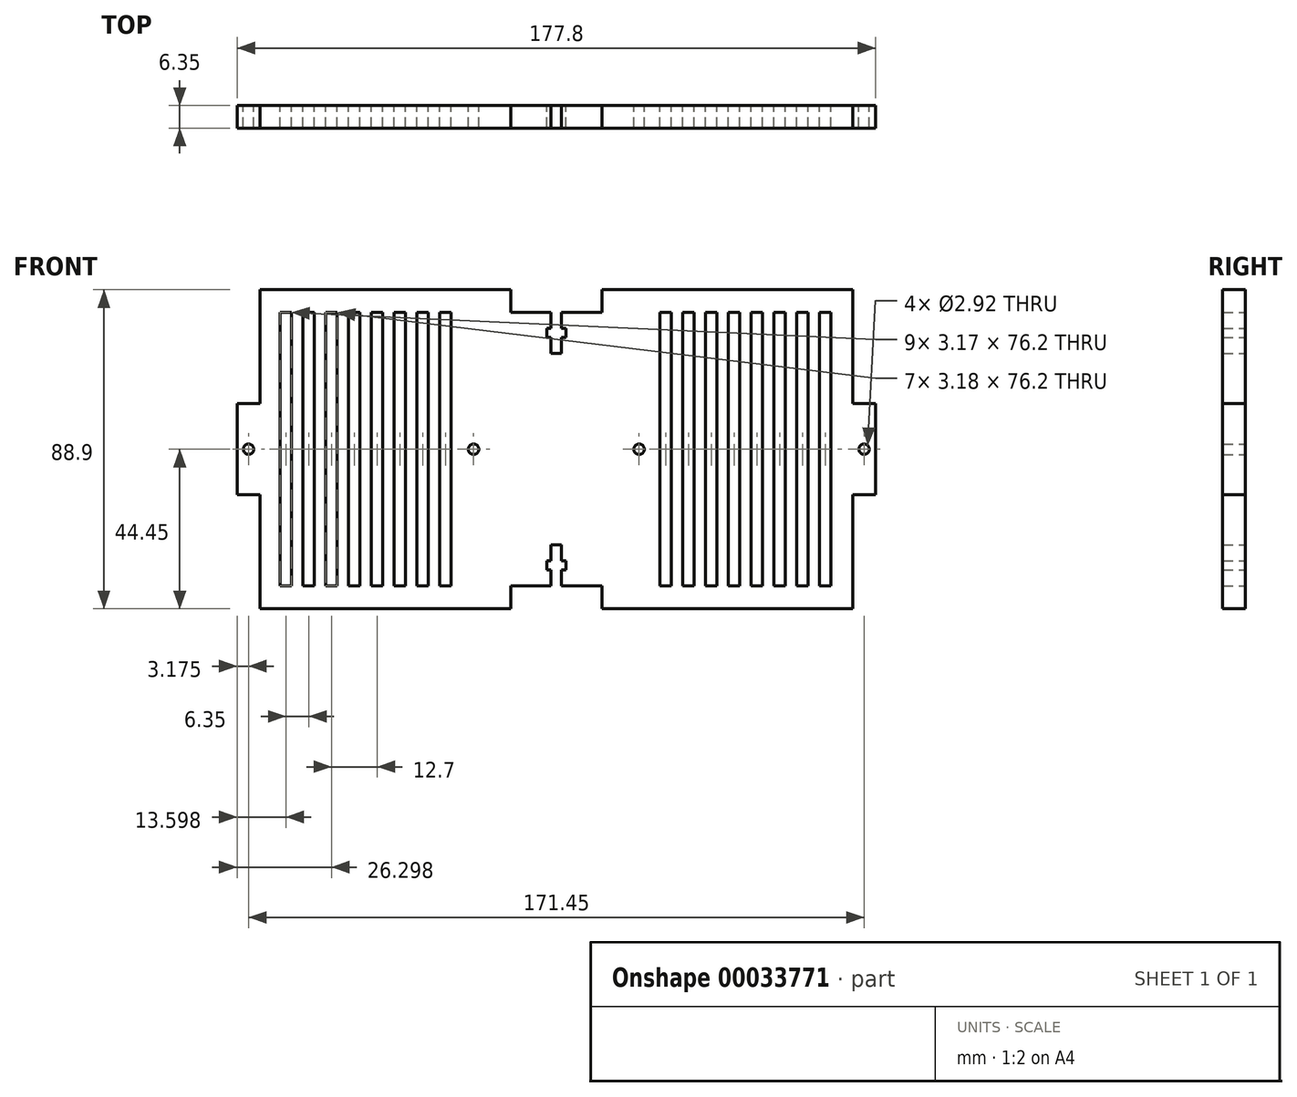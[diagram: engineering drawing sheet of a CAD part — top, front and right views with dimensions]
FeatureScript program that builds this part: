
annotation { "Feature Type Name" : "Feature", "Feature Type Description" : "" }
export const myFeature = defineFeature(function(context is Context, id is Id, definition is map)
    precondition{}
    {
        {
            var Q0;
            Q0=qCreatedBy(makeId("Front.planeOp"),FACE);
            var sketch = newSketch(context, id + "F0", { "sketchPlane" : qUnion([Q0])});
            skLineSegment(sketch, "E0.rect.top", {"start": v(82.55, 44.45) * mm, "end": v(12.7, 44.45) * mm});
            skLineSegment(sketch, "E0.rect.left", {"start": v(88.9, -12.7) * mm, "end": v(88.9, 12.7) * mm});
            skLineSegment(sketch, "E0.rect.right", {"start": v(-88.9, -12.7) * mm, "end": v(-88.9, 12.7) * mm});
            skPoint(sketch, "E0.rect.middle", {"position": v(0, 0) * mm});
            skLineSegment(sketch, "E1", {"start": v(0, 44.45) * mm, "end": v(0, -44.45) * mm, "construction": true});
            skLineSegment(sketch, "E2.0", {"start": v(82.55, 38.1) * mm, "end": v(-82.55, 38.1) * mm, "construction": true});
            skLineSegment(sketch, "E2.1", {"start": v(82.55, -38.1) * mm, "end": v(82.55, 38.1) * mm, "construction": true});
            skLineSegment(sketch, "E2.2", {"start": v(82.55, -38.1) * mm, "end": v(-82.55, -38.1) * mm, "construction": true});
            skLineSegment(sketch, "E2.3", {"start": v(-82.55, -38.1) * mm, "end": v(-82.55, 0) * mm, "construction": true});
            skLineSegment(sketch, "E3.0", {"start": v(-88.9, -12.7) * mm, "end": v(88.9, -12.7) * mm, "construction": true});
            skLineSegment(sketch, "E4.MirrorCS", {"start": v(-88.9, 12.7) * mm, "end": v(88.9, 12.7) * mm, "construction": true});
            skLineSegment(sketch, "E5.MirrorCS", {"start": v(12.7, 44.45) * mm, "end": v(12.7, -44.45) * mm, "construction": true});
            skLineSegment(sketch, "E6", {"start": v(-12.7, 44.45) * mm, "end": v(-12.7, 38.1) * mm, "construction": true});
            skLineSegment(sketch, "E7", {"start": v(-12.7, 38.1) * mm, "end": v(12.7, 38.1) * mm, "construction": true});
            skLineSegment(sketch, "E8", {"start": v(12.7, 38.1) * mm, "end": v(12.7, 44.45) * mm, "construction": true});
            skLineSegment(sketch, "E9.MirrorCS", {"start": v(-12.7, -44.45) * mm, "end": v(-12.7, -38.1) * mm});
            skLineSegment(sketch, "E10.MirrorCS", {"start": v(-12.7, -38.1) * mm, "end": v(-1.46, -38.1) * mm});
            skLineSegment(sketch, "E11.MirrorCS", {"start": v(12.7, -38.1) * mm, "end": v(12.7, -44.45) * mm});
            skLineSegment(sketch, "E12.trimOffspring", {"start": v(-12.7, 44.45) * mm, "end": v(-82.55, 44.45) * mm});
            skLineSegment(sketch, "E13", {"start": v(-12.7, 44.45) * mm, "end": v(-12.7, 38.1) * mm});
            skLineSegment(sketch, "E14", {"start": v(-12.7, 38.1) * mm, "end": v(-1.46, 38.1) * mm});
            skLineSegment(sketch, "E15", {"start": v(12.7, 38.1) * mm, "end": v(12.7, 44.45) * mm});
            skLineSegment(sketch, "E16", {"start": v(-88.9, 12.7) * mm, "end": v(-82.55, 12.7) * mm});
            skLineSegment(sketch, "E17", {"start": v(-82.55, 12.7) * mm, "end": v(-82.55, 44.45) * mm});
            skLineSegment(sketch, "E18.MirrorCS", {"start": v(-88.9, -12.7) * mm, "end": v(-82.55, -12.7) * mm});
            skLineSegment(sketch, "E19.MirrorCS", {"start": v(-82.55, -12.7) * mm, "end": v(-82.55, -44.45) * mm});
            skLineSegment(sketch, "E20.MirrorCS", {"start": v(82.55, 12.7) * mm, "end": v(82.55, 44.45) * mm});
            skLineSegment(sketch, "E21.MirrorCS", {"start": v(88.9, 12.7) * mm, "end": v(82.55, 12.7) * mm});
            skLineSegment(sketch, "E22.MirrorCS", {"start": v(88.9, -12.7) * mm, "end": v(82.55, -12.7) * mm, "construction": true});
            skLineSegment(sketch, "E23.MirrorCS", {"start": v(82.55, -12.7) * mm, "end": v(82.55, -44.45) * mm});
            skLineSegment(sketch, "E24", {"start": v(-88.9, 0) * mm, "end": v(-82.55, 0) * mm, "construction": true});
            skLineSegment(sketch, "E25", {"start": v(82.55, -12.7) * mm, "end": v(88.9, -12.7) * mm});
            skPoint(sketch, "E26.orphan", {"position": v(88.9, 44.45) * mm});
            skPoint(sketch, "E27.orphan", {"position": v(88.9, -44.45) * mm});
            skPoint(sketch, "E28.orphan", {"position": v(-88.9, -44.45) * mm});
            skPoint(sketch, "E29.orphan", {"position": v(-88.9, 44.45) * mm});
            skLineSegment(sketch, "E30", {"start": v(-82.55, 0) * mm, "end": v(-82.55, 38.1) * mm, "construction": true});
            skCircle(sketch, "E31", {"center": v(-85.73, 0) * mm, "radius": 1.46 * mm});
            skCircle(sketch, "E32.MirrorC", {"center": v(85.73, 0) * mm, "radius": 1.46 * mm});
            skLineSegment(sketch, "E33.0", {"start": v(-1.46, 44.45) * mm, "end": v(-1.46, -44.45) * mm, "construction": true});
            skLineSegment(sketch, "E34.MirrorCS", {"start": v(1.46, 44.45) * mm, "end": v(1.46, -44.45) * mm, "construction": true});
            skLineSegment(sketch, "E35", {"start": v(-12.7, 26.67) * mm, "end": v(12.7, 26.67) * mm, "construction": true});
            skLineSegment(sketch, "E36", {"start": v(-12.7, 26.67) * mm, "end": v(-12.7, -44.45) * mm, "construction": true});
            skLineSegment(sketch, "E37", {"start": v(-12.7, 38.1) * mm, "end": v(-12.7, 26.67) * mm, "construction": true});
            skLineSegment(sketch, "E38", {"start": v(-12.7, 32.39) * mm, "end": v(12.7, 32.39) * mm, "construction": true});
            skLineSegment(sketch, "E39.0", {"start": v(-12.7, 31.12) * mm, "end": v(12.7, 31.12) * mm, "construction": true});
            skLineSegment(sketch, "E40.MirrorCS", {"start": v(-12.7, 33.66) * mm, "end": v(12.7, 33.66) * mm, "construction": true});
            skLineSegment(sketch, "E41.0", {"start": v(-2.7, 44.45) * mm, "end": v(-2.7, -44.45) * mm, "construction": true});
            skLineSegment(sketch, "E42.MirrorCS", {"start": v(2.7, 44.45) * mm, "end": v(2.7, -44.45) * mm, "construction": true});
            skLineSegment(sketch, "E43", {"start": v(-1.46, 38.1) * mm, "end": v(-1.46, 33.66) * mm});
            skLineSegment(sketch, "E44", {"start": v(-1.46, 33.66) * mm, "end": v(-2.7, 33.66) * mm});
            skLineSegment(sketch, "E45", {"start": v(-2.7, 33.66) * mm, "end": v(-2.7, 31.12) * mm});
            skLineSegment(sketch, "E46", {"start": v(-2.7, 31.12) * mm, "end": v(-1.46, 31.12) * mm});
            skLineSegment(sketch, "E47", {"start": v(-1.46, 31.12) * mm, "end": v(-1.46, 26.67) * mm});
            skLineSegment(sketch, "E48", {"start": v(-1.46, 26.67) * mm, "end": v(1.46, 26.67) * mm});
            skLineSegment(sketch, "E49", {"start": v(1.46, 26.67) * mm, "end": v(1.46, 31.12) * mm});
            skLineSegment(sketch, "E50", {"start": v(1.46, 31.12) * mm, "end": v(2.7, 31.12) * mm});
            skLineSegment(sketch, "E51", {"start": v(2.7, 31.12) * mm, "end": v(2.7, 33.66) * mm});
            skLineSegment(sketch, "E52", {"start": v(2.7, 33.66) * mm, "end": v(1.46, 33.66) * mm});
            skLineSegment(sketch, "E53", {"start": v(1.46, 33.66) * mm, "end": v(1.46, 38.1) * mm});
            skLineSegment(sketch, "E54.trimOffspring", {"start": v(1.46, 38.1) * mm, "end": v(12.7, 38.1) * mm});
            skLineSegment(sketch, "E55.MirrorCS", {"start": v(-1.46, -38.1) * mm, "end": v(-1.46, -33.66) * mm});
            skLineSegment(sketch, "E56.MirrorCS", {"start": v(-1.46, -33.66) * mm, "end": v(-2.7, -33.66) * mm});
            skLineSegment(sketch, "E57.MirrorCS", {"start": v(-2.7, -33.66) * mm, "end": v(-2.7, -31.12) * mm});
            skLineSegment(sketch, "E58.MirrorCS", {"start": v(-2.7, -31.12) * mm, "end": v(-1.46, -31.12) * mm});
            skLineSegment(sketch, "E59.MirrorCS", {"start": v(-1.46, -31.12) * mm, "end": v(-1.46, -26.67) * mm});
            skLineSegment(sketch, "E60.MirrorCS", {"start": v(-1.46, -26.67) * mm, "end": v(1.46, -26.67) * mm});
            skLineSegment(sketch, "E61.MirrorCS", {"start": v(1.46, -26.67) * mm, "end": v(1.46, -31.12) * mm});
            skLineSegment(sketch, "E62.MirrorCS", {"start": v(1.46, -31.12) * mm, "end": v(2.7, -31.12) * mm});
            skLineSegment(sketch, "E63.MirrorCS", {"start": v(2.7, -31.12) * mm, "end": v(2.7, -33.66) * mm});
            skLineSegment(sketch, "E64.MirrorCS", {"start": v(2.7, -33.66) * mm, "end": v(1.46, -33.66) * mm});
            skLineSegment(sketch, "E65.MirrorCS", {"start": v(1.46, -33.66) * mm, "end": v(1.46, -38.1) * mm});
            skLineSegment(sketch, "E66.trimOffspring", {"start": v(1.46, -38.1) * mm, "end": v(12.7, -38.1) * mm});
            skPoint(sketch, "E67.MirrorCS.end.orphan", {"position": v(82.55, -44.45) * mm});
            skPoint(sketch, "E68.MirrorCS.end.orphan", {"position": v(12.7, -44.45) * mm});
            skPoint(sketch, "E69.MirrorCS.end.orphan", {"position": v(-12.7, -44.45) * mm});
            skLineSegment(sketch, "E70", {"start": v(-82.55, -44.45) * mm, "end": v(-12.7, -44.45) * mm});
            skLineSegment(sketch, "E71", {"start": v(82.55, -44.45) * mm, "end": v(12.7, -44.45) * mm});
            skLineSegment(sketch, "E72", {"start": v(-47.63, 44.45) * mm, "end": v(-47.63, -44.45) * mm, "construction": true});
            skLineSegment(sketch, "E73", {"start": v(47.63, 44.45) * mm, "end": v(47.63, -44.45) * mm, "construction": true});
            skLineSegment(sketch, "E74.0", {"start": v(-27.94, 44.45) * mm, "end": v(-27.94, -44.45) * mm, "construction": true});
            skLineSegment(sketch, "E75.MirrorCS", {"start": v(27.94, 44.45) * mm, "end": v(27.94, -44.45) * mm, "construction": true});
            skLineSegment(sketch, "E76.MirrorCS", {"start": v(20.32, 44.45) * mm, "end": v(20.32, -44.45) * mm, "construction": true});
            skLineSegment(sketch, "E77", {"start": v(-20.32, 0) * mm, "end": v(88.9, 0) * mm, "construction": true});
            skLineSegment(sketch, "E78.0", {"start": v(-21.59, 44.45) * mm, "end": v(-21.59, -44.45) * mm, "construction": true});
            skLineSegment(sketch, "E79.0", {"start": v(-24.51, 44.45) * mm, "end": v(-24.51, -44.45) * mm, "construction": true});
            skLineSegment(sketch, "E80", {"start": v(-24.51, 0) * mm, "end": v(-21.59, 0) * mm, "construction": true});
            skCircle(sketch, "E81", {"center": v(-23.05, 0) * mm, "radius": 1.46 * mm});
            skCircle(sketch, "E82.MirrorC", {"center": v(23.05, 0) * mm, "radius": 1.46 * mm});
            skLineSegment(sketch, "E83.bottom", {"start": v(-76.89, 38.1) * mm, "end": v(-73.71, 38.1) * mm});
            skLineSegment(sketch, "E83.top", {"start": v(-76.89, -38.1) * mm, "end": v(-73.71, -38.1) * mm});
            skLineSegment(sketch, "E83.left", {"start": v(-76.89, 38.1) * mm, "end": v(-76.89, -38.1) * mm});
            skLineSegment(sketch, "E83.right", {"start": v(-73.71, 38.1) * mm, "end": v(-73.71, -38.1) * mm});
            skLineSegment(sketch, "E84.1.0.0", {"start": v(-70.54, 38.1) * mm, "end": v(-67.36, 38.1) * mm});
            skLineSegment(sketch, "E84.1.0.1", {"start": v(-70.54, 38.1) * mm, "end": v(-70.54, -38.1) * mm});
            skLineSegment(sketch, "E84.1.0.2", {"start": v(-67.36, 38.1) * mm, "end": v(-67.36, -38.1) * mm});
            skLineSegment(sketch, "E84.1.0.3", {"start": v(-70.54, -38.1) * mm, "end": v(-67.36, -38.1) * mm});
            skLineSegment(sketch, "E84.2.0.0", {"start": v(-64.19, 38.1) * mm, "end": v(-61.01, 38.1) * mm});
            skLineSegment(sketch, "E84.2.0.1", {"start": v(-64.19, 38.1) * mm, "end": v(-64.19, -38.1) * mm});
            skLineSegment(sketch, "E84.2.0.2", {"start": v(-61.01, 38.1) * mm, "end": v(-61.01, -38.1) * mm});
            skLineSegment(sketch, "E84.2.0.3", {"start": v(-64.19, -38.1) * mm, "end": v(-61.01, -38.1) * mm});
            skLineSegment(sketch, "E84.3.0.0", {"start": v(-57.84, 38.1) * mm, "end": v(-54.66, 38.1) * mm});
            skLineSegment(sketch, "E84.3.0.1", {"start": v(-57.84, 38.1) * mm, "end": v(-57.84, -38.1) * mm});
            skLineSegment(sketch, "E84.3.0.2", {"start": v(-54.66, 38.1) * mm, "end": v(-54.66, -38.1) * mm});
            skLineSegment(sketch, "E84.3.0.3", {"start": v(-57.84, -38.1) * mm, "end": v(-54.66, -38.1) * mm});
            skLineSegment(sketch, "E84.4.0.0", {"start": v(-51.49, 38.1) * mm, "end": v(-48.31, 38.1) * mm});
            skLineSegment(sketch, "E84.4.0.1", {"start": v(-51.49, 38.1) * mm, "end": v(-51.49, -38.1) * mm});
            skLineSegment(sketch, "E84.4.0.2", {"start": v(-48.31, 38.1) * mm, "end": v(-48.31, -38.1) * mm});
            skLineSegment(sketch, "E84.4.0.3", {"start": v(-51.49, -38.1) * mm, "end": v(-48.31, -38.1) * mm});
            skLineSegment(sketch, "E84.5.0.0", {"start": v(-45.14, 38.1) * mm, "end": v(-41.96, 38.1) * mm});
            skLineSegment(sketch, "E84.5.0.1", {"start": v(-45.14, 38.1) * mm, "end": v(-45.14, -38.1) * mm});
            skLineSegment(sketch, "E84.5.0.2", {"start": v(-41.96, 38.1) * mm, "end": v(-41.96, -38.1) * mm});
            skLineSegment(sketch, "E84.5.0.3", {"start": v(-45.14, -38.1) * mm, "end": v(-41.96, -38.1) * mm});
            skLineSegment(sketch, "E84.6.0.0", {"start": v(-38.79, 38.1) * mm, "end": v(-35.61, 38.1) * mm});
            skLineSegment(sketch, "E84.6.0.1", {"start": v(-38.79, 38.1) * mm, "end": v(-38.79, -38.1) * mm});
            skLineSegment(sketch, "E84.6.0.2", {"start": v(-35.61, 38.1) * mm, "end": v(-35.61, -38.1) * mm});
            skLineSegment(sketch, "E84.6.0.3", {"start": v(-38.79, -38.1) * mm, "end": v(-35.61, -38.1) * mm});
            skLineSegment(sketch, "E84.7.0.0", {"start": v(-32.44, 38.1) * mm, "end": v(-29.26, 38.1) * mm});
            skLineSegment(sketch, "E84.7.0.1", {"start": v(-32.44, 38.1) * mm, "end": v(-32.44, -38.1) * mm});
            skLineSegment(sketch, "E84.7.0.2", {"start": v(-29.26, 38.1) * mm, "end": v(-29.26, -38.1) * mm});
            skLineSegment(sketch, "E84.7.0.3", {"start": v(-32.44, -38.1) * mm, "end": v(-29.26, -38.1) * mm});
            skLineSegment(sketch, "E84.direction1", {"start": v(-76.89, 38.1) * mm, "end": v(-70.54, 38.1) * mm, "construction": true});
            skLineSegment(sketch, "E85.bottom", {"start": v(76.52, 38.1) * mm, "end": v(73.35, 38.1) * mm});
            skLineSegment(sketch, "E85.top", {"start": v(76.52, -38.1) * mm, "end": v(73.35, -38.1) * mm});
            skLineSegment(sketch, "E85.left", {"start": v(76.52, 38.1) * mm, "end": v(76.52, -38.1) * mm});
            skLineSegment(sketch, "E85.right", {"start": v(73.35, 38.1) * mm, "end": v(73.35, -38.1) * mm});
            skLineSegment(sketch, "E86.1.0.0", {"start": v(70.17, 38.1) * mm, "end": v(67, 38.1) * mm});
            skLineSegment(sketch, "E86.1.0.1", {"start": v(70.17, 38.1) * mm, "end": v(70.17, -38.1) * mm});
            skLineSegment(sketch, "E86.1.0.2", {"start": v(67, 38.1) * mm, "end": v(67, -38.1) * mm});
            skLineSegment(sketch, "E86.1.0.3", {"start": v(70.17, -38.1) * mm, "end": v(67, -38.1) * mm});
            skLineSegment(sketch, "E86.2.0.0", {"start": v(63.82, 38.1) * mm, "end": v(60.65, 38.1) * mm});
            skLineSegment(sketch, "E86.2.0.1", {"start": v(63.82, 38.1) * mm, "end": v(63.82, -38.1) * mm});
            skLineSegment(sketch, "E86.2.0.2", {"start": v(60.65, 38.1) * mm, "end": v(60.65, -38.1) * mm});
            skLineSegment(sketch, "E86.2.0.3", {"start": v(63.82, -38.1) * mm, "end": v(60.65, -38.1) * mm});
            skLineSegment(sketch, "E86.3.0.0", {"start": v(57.47, 38.1) * mm, "end": v(54.3, 38.1) * mm});
            skLineSegment(sketch, "E86.3.0.1", {"start": v(57.47, 38.1) * mm, "end": v(57.47, -38.1) * mm});
            skLineSegment(sketch, "E86.3.0.2", {"start": v(54.3, 38.1) * mm, "end": v(54.3, -38.1) * mm});
            skLineSegment(sketch, "E86.3.0.3", {"start": v(57.47, -38.1) * mm, "end": v(54.3, -38.1) * mm});
            skLineSegment(sketch, "E86.4.0.0", {"start": v(51.12, 38.1) * mm, "end": v(47.95, 38.1) * mm});
            skLineSegment(sketch, "E86.4.0.1", {"start": v(51.12, 38.1) * mm, "end": v(51.12, -38.1) * mm});
            skLineSegment(sketch, "E86.4.0.2", {"start": v(47.95, 38.1) * mm, "end": v(47.95, -38.1) * mm});
            skLineSegment(sketch, "E86.4.0.3", {"start": v(51.12, -38.1) * mm, "end": v(47.95, -38.1) * mm});
            skLineSegment(sketch, "E86.5.0.0", {"start": v(44.77, 38.1) * mm, "end": v(41.6, 38.1) * mm});
            skLineSegment(sketch, "E86.5.0.1", {"start": v(44.77, 38.1) * mm, "end": v(44.77, -38.1) * mm});
            skLineSegment(sketch, "E86.5.0.2", {"start": v(41.6, 38.1) * mm, "end": v(41.6, -38.1) * mm});
            skLineSegment(sketch, "E86.5.0.3", {"start": v(44.77, -38.1) * mm, "end": v(41.6, -38.1) * mm});
            skLineSegment(sketch, "E86.6.0.0", {"start": v(38.42, 38.1) * mm, "end": v(35.25, 38.1) * mm});
            skLineSegment(sketch, "E86.6.0.1", {"start": v(38.42, 38.1) * mm, "end": v(38.42, -38.1) * mm});
            skLineSegment(sketch, "E86.6.0.2", {"start": v(35.25, 38.1) * mm, "end": v(35.25, -38.1) * mm});
            skLineSegment(sketch, "E86.6.0.3", {"start": v(38.42, -38.1) * mm, "end": v(35.25, -38.1) * mm});
            skLineSegment(sketch, "E86.7.0.0", {"start": v(32.07, 38.1) * mm, "end": v(28.9, 38.1) * mm});
            skLineSegment(sketch, "E86.7.0.1", {"start": v(32.07, 38.1) * mm, "end": v(32.07, -38.1) * mm});
            skLineSegment(sketch, "E86.7.0.2", {"start": v(28.9, 38.1) * mm, "end": v(28.9, -38.1) * mm});
            skLineSegment(sketch, "E86.7.0.3", {"start": v(32.07, -38.1) * mm, "end": v(28.9, -38.1) * mm});
            skLineSegment(sketch, "E86.direction1", {"start": v(73.35, 38.1) * mm, "end": v(67, 38.1) * mm, "construction": true});
            skSolve(sketch);
        }
        {
            var Q0;
            Q0=makeQuery(id+"F0.imprint","IMPRINT",FACE,{"disambiguationData":[TD([[makeQuery(id+"F0.imprint","IMPRINT",EDGE,{"derivedFrom":sQuery(id+"F0.wireOp",EDGE,"E0.rect.top")}),1.0]])]});
            extrude(context, id + "F1", {"entities" : qUnion([Q0]), "depth" : 6.35 * mm});
        }
    });
